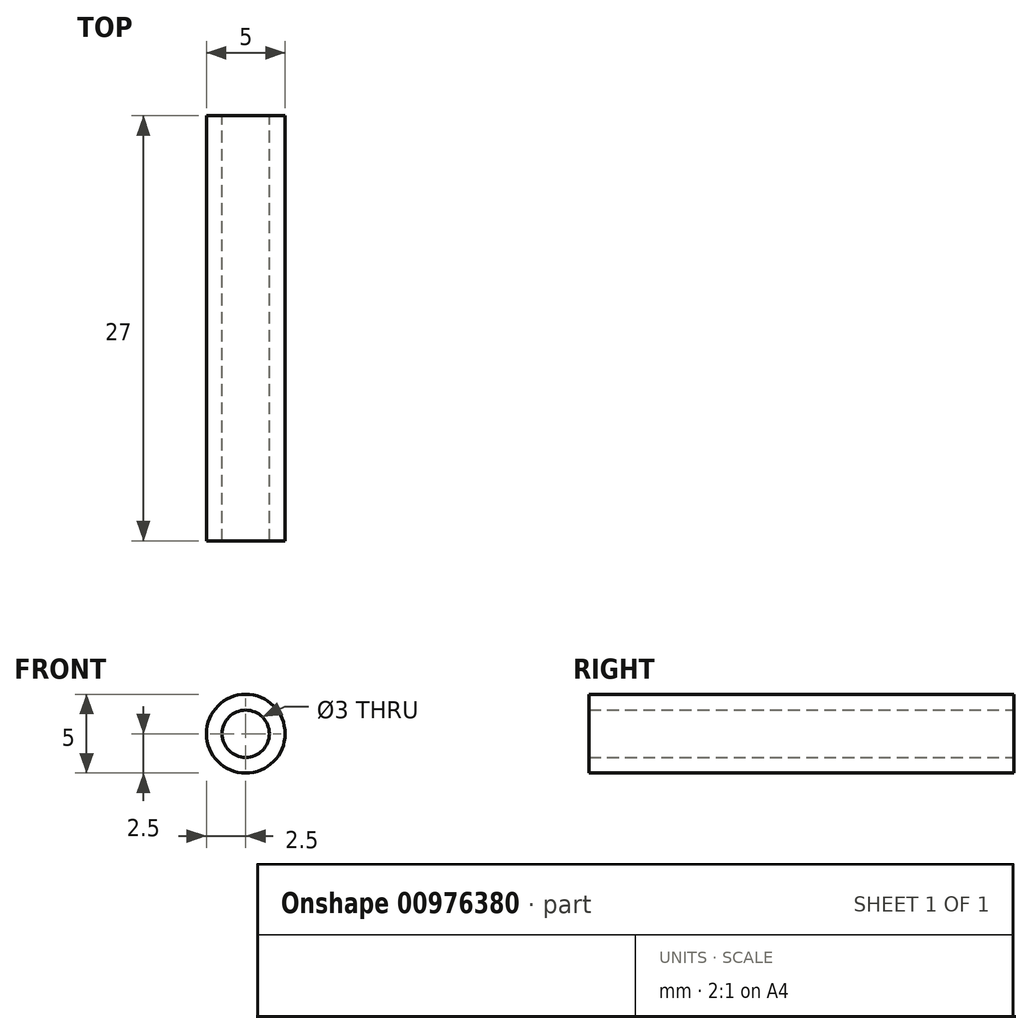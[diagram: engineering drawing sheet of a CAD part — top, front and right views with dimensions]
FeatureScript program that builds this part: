
annotation { "Feature Type Name" : "Feature", "Feature Type Description" : "" }
export const myFeature = defineFeature(function(context is Context, id is Id, definition is map)
    precondition{}
    {
        {
            var Q0;
            Q0=qCreatedBy(makeId("Front.planeOp"),FACE);
            var sketch = newSketch(context, id + "F0", { "sketchPlane" : qUnion([Q0])});
            skCircle(sketch, "E0", {"center": v(0, 0) * mm, "radius": 2.5 * mm});
            skCircle(sketch, "E1", {"center": v(0, 0) * mm, "radius": 1.5 * mm});
            skSolve(sketch);
        }
        {
            var Q0;
            Q0 = qSketchRegion(id + "F0", true);
            extrude(context, id + "F1", {"entities" : qUnion([Q0]), "depth" : 27 * mm, "offsetDistance" : 25 * mm});
        }
    });
